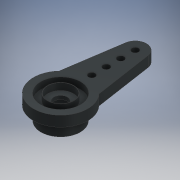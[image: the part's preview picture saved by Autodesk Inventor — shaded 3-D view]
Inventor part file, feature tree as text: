
AUTODESK INVENTOR PART (.ipt)
format: ipt  version: 2019 (Build 230136000, 136)  size: 161,792 bytes
history: native  units: mm
features: extrude x5, sketch x5
ambient origin geometry x8: Origin, YZ Plane, XZ Plane, XY Plane, X Axis, Y Axis, Z Axis, Center Point
bodies: Solid1 (feature_tree)
feature tree (10):
  extrude  "Extrusion1"  Depth=3.0mm TaperAngle=0.0deg
  extrude  "Extrusion2"  Depth=3.0mm TaperAngle=0.0deg
  extrude  "Extrusion3"  Depth=8.8mm
  extrude  "Extrusion4"  Depth=1.5mm
  extrude  "Extrusion5"  Depth=1.5mm
  sketch  "Sketch1"  dims[d0=8.7mm d1=3.0mm d2=0.0mm]
  sketch  "Sketch2"  dims[d3=6.0mm d4=3.0mm d5=0.0mm]
  sketch  "Sketch3"  dims[d6=12.0mm d8=8.8mm]
  sketch  "Sketch4"  dims[d10=1.5mm d13=1.5mm]
  sketch  "Sketch5"  dims[d14=1.5mm d15=1.5mm d20=2.3mm d21=0.0mm d22=5.7mm d23=8.8mm d24=5.9mm d25=1.5mm d26=0.0mm d27=3.0mm d28=1.5mm d29=0.0mm]
